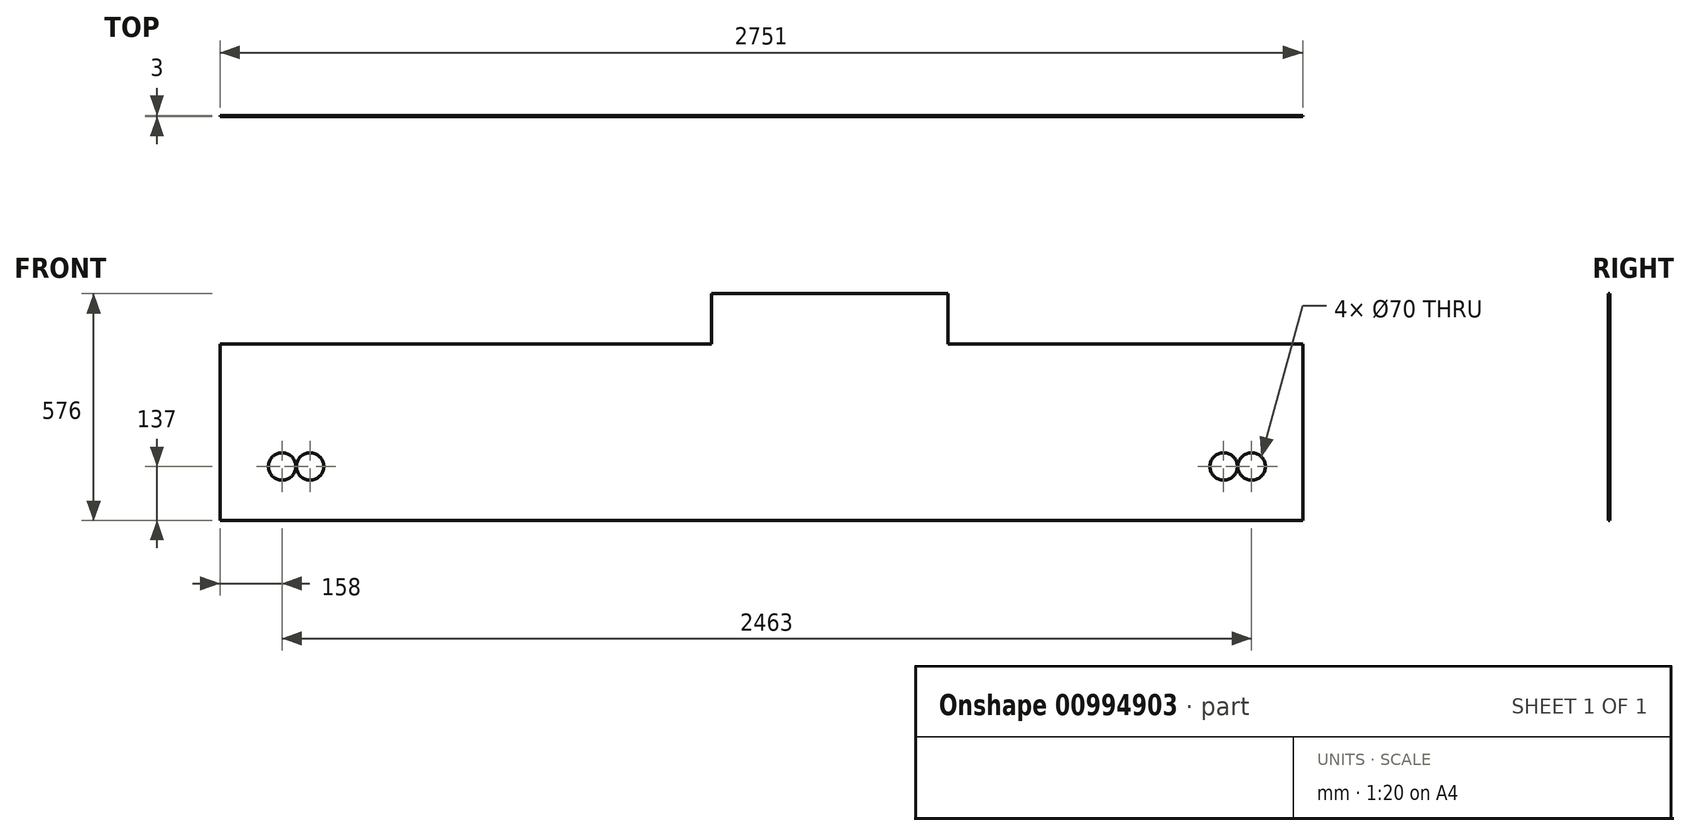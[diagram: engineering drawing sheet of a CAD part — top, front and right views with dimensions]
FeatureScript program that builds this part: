
annotation { "Feature Type Name" : "Feature", "Feature Type Description" : "" }
export const myFeature = defineFeature(function(context is Context, id is Id, definition is map)
    precondition{}
    {
        {
            var Q0;
            Q0=qCreatedBy(makeId("Front.planeOp"), FACE);
            var sketch = newSketch(context, id + "F0", { "sketchPlane" : qUnion([Q0])});
            skLineSegment(sketch, "E0.bottom", {"start": v(0, 0) * mm, "end": v(-2751, 0) * mm});
            skLineSegment(sketch, "E0.top", {"start": v(0, 448) * mm, "end": v(-902, 448) * mm});
            skLineSegment(sketch, "E0.left", {"start": v(0, 0) * mm, "end": v(0, 448) * mm});
            skLineSegment(sketch, "E0.right", {"start": v(-2751, 0) * mm, "end": v(-2751, 448) * mm});
            skCircle(sketch, "E1", {"center": v(-201, 137) * mm, "radius": 35 * mm});
            skCircle(sketch, "E2", {"center": v(-130, 137) * mm, "radius": 35 * mm});
            skCircle(sketch, "E3", {"center": v(-2593, 137) * mm, "radius": 35 * mm});
            skCircle(sketch, "E4", {"center": v(-2522, 137) * mm, "radius": 35 * mm});
            skLineSegment(sketch, "E5.top", {"start": v(-1502, 576) * mm, "end": v(-902, 576) * mm});
            skLineSegment(sketch, "E5.left", {"start": v(-1502, 448) * mm, "end": v(-1502, 576) * mm});
            skLineSegment(sketch, "E5.right", {"start": v(-902, 448) * mm, "end": v(-902, 576) * mm});
            skLineSegment(sketch, "E6.trimOffspring", {"start": v(-1502, 448) * mm, "end": v(-2751, 448) * mm});
            skSolve(sketch);
        }
        {
            var Q0;
            Q0 = qSketchRegion(id + "F0", true);
            extrude(context, id + "F1", {"entities" : qUnion([Q0]), "depth" : 3 * mm, "offsetDistance" : 25 * mm});
        }
    });
